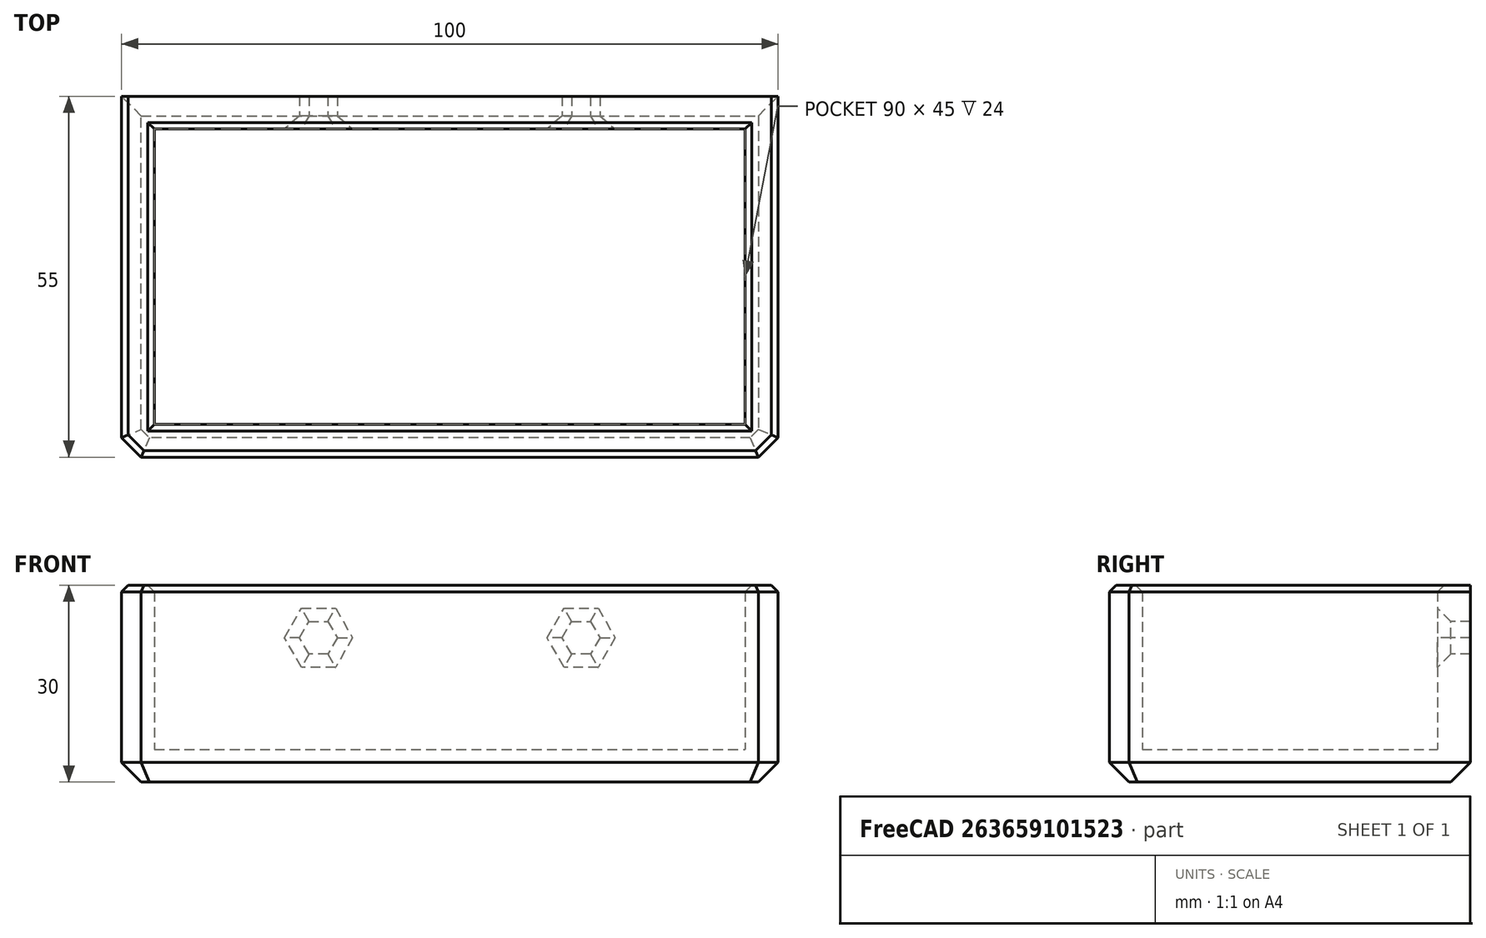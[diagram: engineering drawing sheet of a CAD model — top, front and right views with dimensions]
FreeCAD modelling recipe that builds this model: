
FCSTD DOCUMENT  (FreeCAD 0.19R)
Label: TapeBed
License: All rights reserved
LicenseURL: http://en.wikipedia.org/wiki/All_rights_reserved
objects: PartDesign::Chamfer×4, Sketcher::SketchObject×3, PartDesign::Pocket×2, PartDesign::Pad×1, PartDesign::Body×1, Mesh::Feature×1
note: 18 computed .brp shape members not serialized (recipe doc carries the construction recipe); baked Part::Feature solids carry a one-line shape summary decoded from their .brp

FEATURE [Sketcher::SketchObject] Sketch
  FullyConstrained = true
  MapMode = 5
  Support = -> [XY_Plane]
  sketch-geometry (4):
    g0: LineSegment StartX=-50 StartY=27.5 StartZ=0 EndX=50 EndY=27.5 EndZ=0
    g1: LineSegment StartX=50 StartY=27.5 StartZ=0 EndX=50 EndY=-27.5 EndZ=0
    g2: LineSegment StartX=50 StartY=-27.5 StartZ=0 EndX=-50 EndY=-27.5 EndZ=0
    g3: LineSegment StartX=-50 StartY=-27.5 StartZ=0 EndX=-50 EndY=27.5 EndZ=0
  constraints (11):
    c: Coincident(g0,g1)
    c: Coincident(g1,g2)
    c: Coincident(g2,g3)
    c: Coincident(g3,g0)
    c: Horizontal(g0)
    c: Horizontal(g2)
    c: Vertical(g1)
    c: Vertical(g3)
    c: Distance(g1) = 55
    c: Distance(g0) = 100
    c: Symmetric(g1,g0,g-1)
FEATURE [PartDesign::Pad] Pad
  Direction = (1,1,1)
  Length = 30
  Length2 = 100
  Profile = -> Sketch
  Type = 0
FEATURE [Sketcher::SketchObject] Sketch001
  FullyConstrained = true
  MapMode = 5
  Placement = pos=(0,0,30) rot=(0,0,1;0rad)
  Support = -> [Pad]
  sketch-geometry (4):
    g0: LineSegment StartX=-45 StartY=22.5 StartZ=0 EndX=45 EndY=22.5 EndZ=0
    g1: LineSegment StartX=45 StartY=22.5 StartZ=0 EndX=45 EndY=-22.5 EndZ=0
    g2: LineSegment StartX=45 StartY=-22.5 StartZ=0 EndX=-45 EndY=-22.5 EndZ=0
    g3: LineSegment StartX=-45 StartY=-22.5 StartZ=0 EndX=-45 EndY=22.5 EndZ=0
  constraints (11):
    c: Coincident(g0,g1)
    c: Coincident(g1,g2)
    c: Coincident(g2,g3)
    c: Coincident(g3,g0)
    c: Horizontal(g0)
    c: Horizontal(g2)
    c: Vertical(g1)
    c: Vertical(g3)
    c: Symmetric(g1,g0,g-1)
    c: Distance(g0) = 90
    c: Distance(g1) = 45
FEATURE [PartDesign::Pocket] Pocket
  BaseFeature = -> Pad
  Length = 25
  Length2 = 100
  Profile = -> Sketch001
  Type = 0
FEATURE [PartDesign::Chamfer] Chamfer
  Angle = 45
  Base = -> Pocket [Edge8,Edge5]
  BaseFeature = -> Pocket
  ChamferType = 0
  FlipDirection = false
  Size = 3
  Size2 = 1
  SupportTransform = false
FEATURE [PartDesign::Chamfer] Chamfer001
  Angle = 45
  Base = -> Chamfer [Face2]
  BaseFeature = -> Chamfer
  ChamferType = 0
  FlipDirection = false
  Size = 3
  Size2 = 1
  SupportTransform = false
FEATURE [PartDesign::Chamfer] Chamfer002
  Angle = 45
  Base = -> Chamfer001 [Edge3,Edge6,Edge12,Edge14,Edge13,Edge16,Edge17,Edge18,Edge15]
  BaseFeature = -> Chamfer001
  ChamferType = 0
  FlipDirection = false
  Size = 1
  Size2 = 1
  SupportTransform = false
FEATURE [Sketcher::SketchObject] Sketch002
  FullyConstrained = true
  MapMode = 5
  Placement = pos=(0,27.5,0) rot=(0,0.707107,0.707107;3.14159rad)
  Support = -> [Chamfer002]
  sketch-geometry (14):
    g0: LineSegment StartX=-18.5566 StartY=19.5 StartZ=0 EndX=-17.1132 EndY=22 EndZ=0
    g1: LineSegment StartX=-17.1132 StartY=22 StartZ=0 EndX=-18.5566 EndY=24.5 EndZ=0
    g2: LineSegment StartX=-18.5566 StartY=24.5 StartZ=0 EndX=-21.4434 EndY=24.5 EndZ=0
    g3: LineSegment StartX=-21.4434 StartY=24.5 StartZ=0 EndX=-22.8868 EndY=22 EndZ=0
    g4: LineSegment StartX=-22.8868 StartY=22 StartZ=0 EndX=-21.4434 EndY=19.5 EndZ=0
    g5: LineSegment StartX=-21.4434 StartY=19.5 StartZ=0 EndX=-18.5566 EndY=19.5 EndZ=0
    g6: Circle CenterX=-20 CenterY=22 CenterZ=0 NormalX=0 NormalY=0 NormalZ=1 AngleXU=0 Radius=2.88675
    g7: LineSegment StartX=21.4434 StartY=19.5 StartZ=0 EndX=22.8868 EndY=22 EndZ=0
    g8: LineSegment StartX=22.8868 StartY=22 StartZ=0 EndX=21.4434 EndY=24.5 EndZ=0
    g9: LineSegment StartX=21.4434 StartY=24.5 StartZ=0 EndX=18.5566 EndY=24.5 EndZ=0
    g10: LineSegment StartX=18.5566 StartY=24.5 StartZ=0 EndX=17.1132 EndY=22 EndZ=0
    g11: LineSegment StartX=17.1132 StartY=22 StartZ=0 EndX=18.5566 EndY=19.5 EndZ=0
    g12: LineSegment StartX=18.5566 StartY=19.5 StartZ=0 EndX=21.4434 EndY=19.5 EndZ=0
    g13: Circle CenterX=20 CenterY=22 CenterZ=0 NormalX=0 NormalY=0 NormalZ=1 AngleXU=0 Radius=2.88675
  constraints (33):
    c: Coincident(g0,g1)
    c: Coincident(g1,g2)
    c: Coincident(g2,g3)
    c: Coincident(g3,g4)
    c: Coincident(g4,g5)
    c: Coincident(g5,g0)
    c: Equal(g0, g1-g5) x5
    c: PointOnObject(g0,g6)
    c: PointOnObject(g1,g6)
    c: PointOnObject(g2,g6)
    c: PointOnObject(g3,g6)
    c: PointOnObject(g4,g6)
    c: PointOnObject(g5,g6)
    c: Coincident(g7,g8)
    c: Coincident(g8,g9)
    c: Coincident(g9,g10)
    c: Coincident(g10,g11)
    c: Coincident(g11,g12)
    c: Coincident(g12,g7)
    c: Equal(g7, g8-g12) x5
    c: PointOnObject(g7,g13)
    c: PointOnObject(g8,g13)
    c: PointOnObject(g9,g13)
    c: PointOnObject(g10,g13)
    c: PointOnObject(g11,g13)
    c: PointOnObject(g12,g13)
    c: Symmetric(g13,g6,g-2)
    c: Distance(g8,g10) = 5
    c: Equal(g10,g2)
    c: Horizontal(g9)
    c: DistanceY(g6) = 22
    c: DistanceX(g13) = 20
    c: Horizontal(g2)
FEATURE [PartDesign::Pocket] Pocket001
  BaseFeature = -> Chamfer002
  Length = 5
  Length2 = 100
  Profile = -> Sketch002
  Type = 0
FEATURE [PartDesign::Chamfer] Chamfer003
  Angle = 45
  Base = -> Pocket001 [Edge61,Edge59,Edge63,Edge64,Edge55,Edge57,Edge67,Edge69,Edge71,Edge73,Edge75,Edge76]
  BaseFeature = -> Pocket001
  ChamferType = 0
  FlipDirection = false
  Size = 2
  Size2 = 1
  SupportTransform = false
FEATURE [PartDesign::Body] Body
  Group = -> [Sketch,Pad,Sketch001,Pocket,Chamfer,Chamfer001,Chamfer002,Sketch002,Pocket001,Chamfer003]
  Origin = -> Origin
  Tip = -> Chamfer003
FEATURE [Mesh::Feature] Mesh  label="Chamfer003 (Meshed)"
